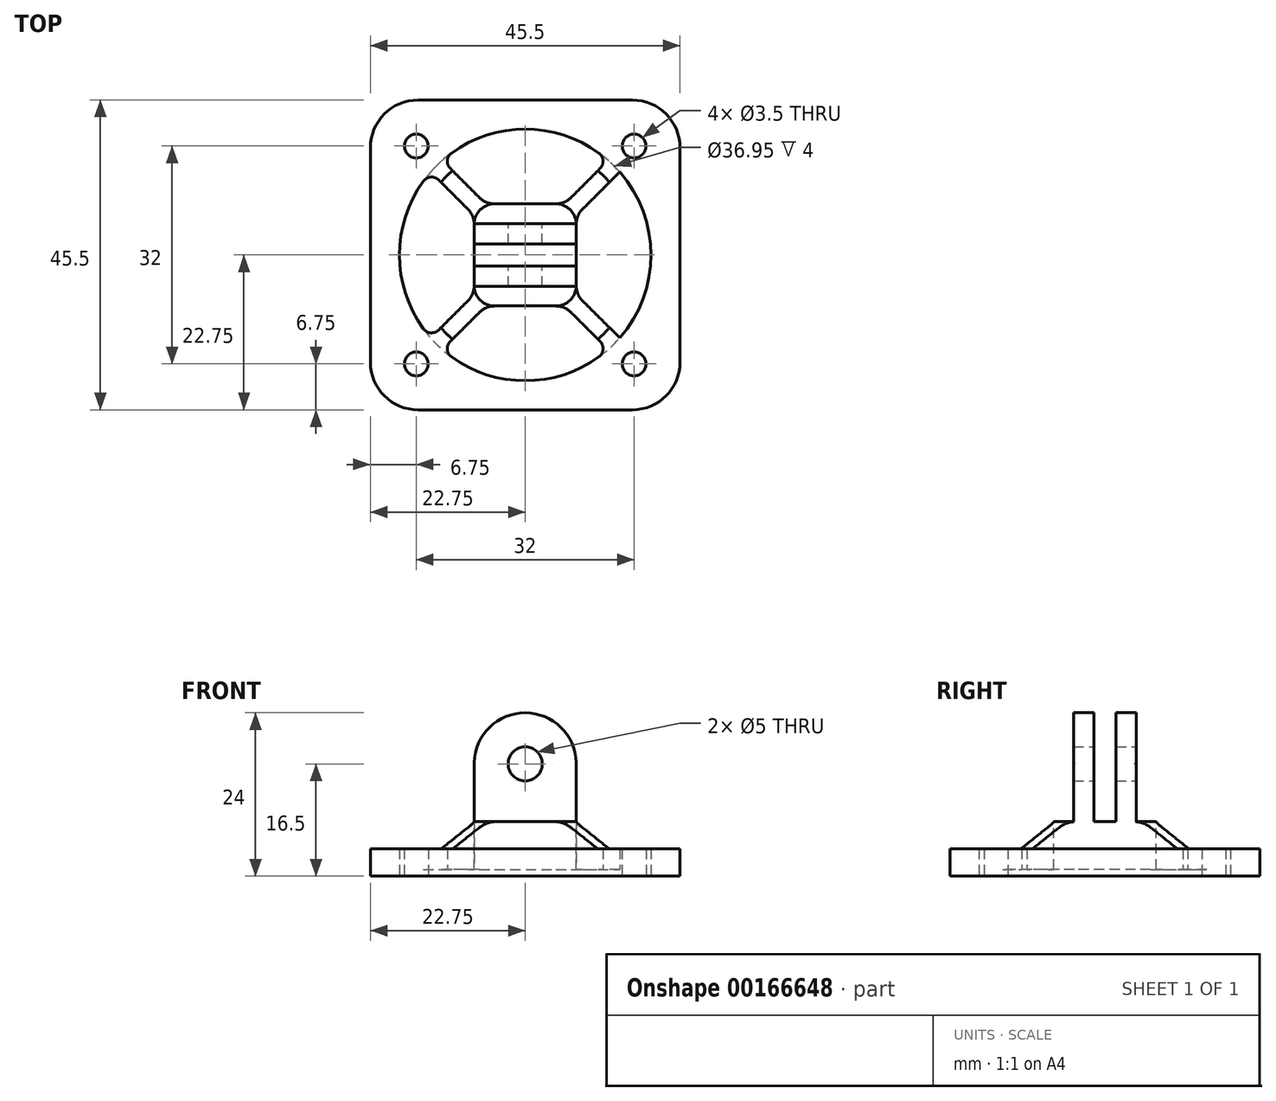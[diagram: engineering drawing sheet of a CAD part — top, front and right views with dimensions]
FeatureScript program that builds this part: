
annotation { "Feature Type Name" : "Feature", "Feature Type Description" : "" }
export const myFeature = defineFeature(function(context is Context, id is Id, definition is map)
    precondition{}
    {
        {
            var Q0;
            Q0=qCreatedBy(makeId("Top.planeOp"),FACE);
            var sketch = newSketch(context, id + "F0", { "sketchPlane" : qUnion([Q0])});
            skLineSegment(sketch, "E0.bottom", {"start": v(16, -16) * mm, "end": v(-16, -16) * mm, "construction": true});
            skLineSegment(sketch, "E0.top", {"start": v(16, 16) * mm, "end": v(-16, 16) * mm, "construction": true});
            skLineSegment(sketch, "E0.left", {"start": v(16, -16) * mm, "end": v(16, 16) * mm, "construction": true});
            skLineSegment(sketch, "E0.right", {"start": v(-16, -16) * mm, "end": v(-16, 16) * mm, "construction": true});
            skPoint(sketch, "E0.middle", {"position": v(0, 0) * mm});
            skLineSegment(sketch, "E1.bottom", {"start": v(22.75, -22.75) * mm, "end": v(-22.75, -22.75) * mm});
            skLineSegment(sketch, "E1.top", {"start": v(22.75, 22.75) * mm, "end": v(-22.75, 22.75) * mm});
            skLineSegment(sketch, "E1.left", {"start": v(22.75, -22.75) * mm, "end": v(22.75, 22.75) * mm});
            skLineSegment(sketch, "E1.right", {"start": v(-22.75, -22.75) * mm, "end": v(-22.75, 22.75) * mm});
            skCircle(sketch, "E2", {"center": v(-16, 16) * mm, "radius": 1.75 * mm, "construction": true});
            skCircle(sketch, "E3", {"center": v(16, 16) * mm, "radius": 1.75 * mm, "construction": true});
            skCircle(sketch, "E4", {"center": v(16, -16) * mm, "radius": 1.75 * mm, "construction": true});
            skCircle(sketch, "E5", {"center": v(-16, -16) * mm, "radius": 1.75 * mm, "construction": true});
            skCircle(sketch, "E6", {"center": v(0, 0) * mm, "radius": 18.48 * mm});
            skCircle(sketch, "E7", {"center": v(0, 0) * mm, "radius": 7.5 * mm});
            skLineSegment(sketch, "E8", {"start": v(0, 0) * mm, "end": v(16, 16) * mm, "construction": true});
            skLineSegment(sketch, "E9", {"start": v(6.08, 4.39) * mm, "end": v(13.89, 12.19) * mm});
            skLineSegment(sketch, "E10.MirrorCS", {"start": v(4.39, 6.08) * mm, "end": v(12.19, 13.89) * mm});
            skLineSegment(sketch, "E11.1.0", {"start": v(6.08, -4.39) * mm, "end": v(13.89, -12.19) * mm});
            skLineSegment(sketch, "E11.1.1", {"start": v(4.39, -6.08) * mm, "end": v(12.19, -13.89) * mm});
            skLineSegment(sketch, "E11.2.0", {"start": v(-4.39, -6.08) * mm, "end": v(-12.19, -13.89) * mm});
            skLineSegment(sketch, "E11.2.1", {"start": v(-6.08, -4.39) * mm, "end": v(-13.89, -12.19) * mm});
            skLineSegment(sketch, "E11.3.0", {"start": v(-6.08, 4.39) * mm, "end": v(-13.89, 12.19) * mm});
            skLineSegment(sketch, "E11.3.1", {"start": v(-4.39, 6.08) * mm, "end": v(-12.19, 13.89) * mm});
            skLineSegment(sketch, "E11.anchor1", {"start": v(0, 0) * mm, "end": v(4.39, 6.08) * mm, "construction": true});
            skLineSegment(sketch, "E11.anchor2", {"start": v(0, 0) * mm, "end": v(-6.08, 4.39) * mm, "construction": true});
            skSolve(sketch);
        }
        {
            var Q0;
            Q0=makeQuery(id+"F0.imprint","IMPRINT",FACE,{"disambiguationData":[TD([[makeQuery(id+"F0.imprint","IMPRINT",EDGE,{"derivedFrom":sQuery(id+"F0.wireOp",EDGE,"E1.bottom")}),-1.0]])]});
            extrude(context, id + "F1", {"entities" : qUnion([Q0]), "depth" : 3 * mm});
        }
        {
            var Q0;
            {var subQ0=sQuery(id+"F0.wireOp",EDGE,"E7");var subQ8=makeQuery(id+"F0.imprint","INTERSECT",VERTEX,{"derivedFrom":[subQ0,sQuery(id+"F0.wireOp",EDGE,"E9")]});Q0=makeQuery(id+"F0.imprint","IMPRINT",FACE,{"disambiguationData":[TD([[makeQuery(id+"F0.imprint","IMPRINT",EDGE,{"disambiguationData":[TD([[subQ8,-1.0]])],"derivedFrom":subQ0}),1.0]])]});}
            var Q1;
            {var subQ0=sQuery(id+"F0.wireOp",EDGE,"E11.3.0");Q1=makeQuery(id+"F0.imprint","IMPRINT",FACE,{"disambiguationData":[TD([[makeQuery(id+"F0.imprint","IMPRINT",EDGE,{"derivedFrom":subQ0}),-1.0]])]});}
            var Q2;
            Q2=makeQuery(id+"F0.imprint","IMPRINT",FACE,{"disambiguationData":[TD([[makeQuery(id+"F0.imprint","IMPRINT",EDGE,{"derivedFrom":sQuery(id+"F0.wireOp",EDGE,"E1.bottom")}),-1.0]])]});
            var Q3;
            {var subQ0=sQuery(id+"F0.wireOp",EDGE,"E9");Q3=makeQuery(id+"F0.imprint","IMPRINT",FACE,{"disambiguationData":[TD([[makeQuery(id+"F0.imprint","IMPRINT",EDGE,{"derivedFrom":subQ0}),1.0]])]});}
            var Q4;
            {var subQ0=sQuery(id+"F0.wireOp",EDGE,"E11.1.0");Q4=makeQuery(id+"F0.imprint","IMPRINT",FACE,{"disambiguationData":[TD([[makeQuery(id+"F0.imprint","IMPRINT",EDGE,{"derivedFrom":subQ0}),-1.0]])]});}
            var Q5;
            {var subQ0=sQuery(id+"F0.wireOp",EDGE,"E11.2.0");Q5=makeQuery(id+"F0.imprint","IMPRINT",FACE,{"disambiguationData":[TD([[makeQuery(id+"F0.imprint","IMPRINT",EDGE,{"derivedFrom":subQ0}),-1.0]])]});}
            extrude(context, id + "F2", {"entities" : qUnion([Q0, Q1, Q2, Q3, Q4, Q5]), "operationType" : NewBodyOperationType.ADD, "depth" : 3 * mm});
        }
        {
            var Q0;
            Q0=makeQuery(id+"F0.imprint","IMPRINT",FACE,{"disambiguationData":[TD([[makeQuery(id+"F0.imprint","IMPRINT",EDGE,{"derivedFrom":sQuery(id+"F0.wireOp",EDGE,"E1.bottom")}),-1.0]])]});
            extrude(context, id + "F3", {"entities" : qUnion([Q0]), "operationType" : NewBodyOperationType.ADD, "oppositeDirection" : true, "depth" : 1 * mm});
        }
        {
            var Q0;
            Q0=makeQuery(id+"F3.opExtrude","CAP_FACE",FACE,{"disambiguationData":[OSD([sQuery(id+"F0.wireOp",EDGE,"E1.bottom"),sQuery(id+"F0.wireOp",EDGE,"E1.top"),sQuery(id+"F0.wireOp",EDGE,"E1.left"),sQuery(id+"F0.wireOp",EDGE,"E1.right"),sQuery(id+"F0.wireOp",EDGE,"E6")])],"isStart":false});
            var sketch = newSketch(context, id + "F4", { "sketchPlane" : qUnion([Q0])});
            skPoint(sketch, "E12.0", {"position": v(-16, 16) * mm});
            skPoint(sketch, "E12.1", {"position": v(16, 16) * mm});
            skPoint(sketch, "E12.2", {"position": v(16, -16) * mm});
            skPoint(sketch, "E12.3", {"position": v(-16, -16) * mm});
            skSolve(sketch);
        }
        {
            var Q0;
            Q0=sQuery(id+"F4.wireOp",VERTEX,"E12.0");
            var Q1;
            Q1=sQuery(id+"F4.wireOp",VERTEX,"E12.3");
            var Q2;
            Q2=sQuery(id+"F4.wireOp",VERTEX,"E12.2");
            var Q3;
            Q3=sQuery(id+"F4.wireOp",VERTEX,"E12.1");
            var Q4;
            Q4=makeQuery(id+"F1.opExtrude","SWEPT_BODY",BODY,{"disambiguationData":[OSD([sQuery(id+"F0.wireOp",EDGE,"E1.bottom"),sQuery(id+"F0.wireOp",EDGE,"E1.top"),sQuery(id+"F0.wireOp",EDGE,"E1.left"),sQuery(id+"F0.wireOp",EDGE,"E1.right"),sQuery(id+"F0.wireOp",EDGE,"E6")])]});
            hole(context, id + "F5", {"style" : HoleStyle.SIMPLE, "endStyle" : HoleEndStyle.THROUGH, "holeDiameter" : 3.5 * mm, "locations" : qUnion([Q0, Q1, Q2, Q3]), "scope" : qUnion([Q4]), "isTappedThrough" : true});
        }
        {
            var Q0;
            Q0=makeQuery(id+"F2.opExtrude","SWEPT_EDGE",EDGE,{"disambiguationData":[OSD([sQuery(id+"F0.wireOp",EDGE,"E7"),sQuery(id+"F0.wireOp",EDGE,"E11.1.1")])]});
            var Q1;
            Q1=makeQuery(id+"F2.opExtrude","SWEPT_EDGE",EDGE,{"disambiguationData":[OSD([sQuery(id+"F0.wireOp",EDGE,"E7"),sQuery(id+"F0.wireOp",EDGE,"E11.2.0")])]});
            var Q2;
            Q2=makeQuery(id+"F2.opExtrude","SWEPT_EDGE",EDGE,{"disambiguationData":[OSD([sQuery(id+"F0.wireOp",EDGE,"E7"),sQuery(id+"F0.wireOp",EDGE,"E11.2.1")])]});
            var Q3;
            Q3=makeQuery(id+"F2.opExtrude","SWEPT_EDGE",EDGE,{"disambiguationData":[OSD([sQuery(id+"F0.wireOp",EDGE,"E7"),sQuery(id+"F0.wireOp",EDGE,"E11.3.0")])]});
            var Q4;
            Q4=makeQuery(id+"F2.opExtrude","SWEPT_EDGE",EDGE,{"disambiguationData":[OSD([sQuery(id+"F0.wireOp",EDGE,"E7"),sQuery(id+"F0.wireOp",EDGE,"E11.3.1")])]});
            var Q5;
            Q5=makeQuery(id+"F2.opExtrude","SWEPT_EDGE",EDGE,{"disambiguationData":[OSD([sQuery(id+"F0.wireOp",EDGE,"E7"),sQuery(id+"F0.wireOp",EDGE,"E10.MirrorCS")])]});
            var Q6;
            Q6=makeQuery(id+"F2.opExtrude","SWEPT_EDGE",EDGE,{"disambiguationData":[OSD([sQuery(id+"F0.wireOp",EDGE,"E7"),sQuery(id+"F0.wireOp",EDGE,"E9")])]});
            var Q7;
            Q7=makeQuery(id+"F2.opExtrude","SWEPT_EDGE",EDGE,{"disambiguationData":[OSD([sQuery(id+"F0.wireOp",EDGE,"E7"),sQuery(id+"F0.wireOp",EDGE,"E11.1.0")])]});
            var Q8;
            Q8=makeQuery(id+"F2.opExtrude","SWEPT_EDGE",EDGE,{"disambiguationData":[OSD([sQuery(id+"F0.wireOp",EDGE,"E6"),sQuery(id+"F0.wireOp",EDGE,"E11.3.1")])]});
            var Q9;
            Q9=makeQuery(id+"F2.opExtrude","SWEPT_EDGE",EDGE,{"disambiguationData":[OSD([sQuery(id+"F0.wireOp",EDGE,"E6"),sQuery(id+"F0.wireOp",EDGE,"E11.3.0")])]});
            var Q10;
            Q10=makeQuery(id+"F2.opExtrude","SWEPT_EDGE",EDGE,{"disambiguationData":[OSD([sQuery(id+"F0.wireOp",EDGE,"E6"),sQuery(id+"F0.wireOp",EDGE,"E11.2.1")])]});
            var Q11;
            Q11=makeQuery(id+"F2.opExtrude","SWEPT_EDGE",EDGE,{"disambiguationData":[OSD([sQuery(id+"F0.wireOp",EDGE,"E6"),sQuery(id+"F0.wireOp",EDGE,"E11.2.0")])]});
            var Q12;
            Q12=makeQuery(id+"F2.opExtrude","SWEPT_EDGE",EDGE,{"disambiguationData":[OSD([sQuery(id+"F0.wireOp",EDGE,"E6"),sQuery(id+"F0.wireOp",EDGE,"E11.1.0")])]});
            var Q13;
            Q13=makeQuery(id+"F2.opExtrude","SWEPT_EDGE",EDGE,{"disambiguationData":[OSD([sQuery(id+"F0.wireOp",EDGE,"E6"),sQuery(id+"F0.wireOp",EDGE,"E11.1.1")])]});
            var Q14;
            Q14=makeQuery(id+"F2.opExtrude","SWEPT_EDGE",EDGE,{"disambiguationData":[OSD([sQuery(id+"F0.wireOp",EDGE,"E6"),sQuery(id+"F0.wireOp",EDGE,"E9")])]});
            var Q15;
            Q15=makeQuery(id+"F2.opExtrude","SWEPT_EDGE",EDGE,{"disambiguationData":[OSD([sQuery(id+"F0.wireOp",EDGE,"E6"),sQuery(id+"F0.wireOp",EDGE,"E10.MirrorCS")])]});
            fillet(context, id + "F6", {"entities" : qUnion([Q0, Q1, Q2, Q3, Q4, Q5, Q6, Q7, Q8, Q9, Q10, Q11, Q12, Q13, Q14, Q15]), "radius" : 1.5 * mm, "tangentPropagation" : true, "allowEdgeOverflow" : false});
        }
        {
            var Q0;
            {var subQ0=sQuery(id+"F0.wireOp",EDGE,"E1.right");var subQ1=sQuery(id+"F0.wireOp",EDGE,"E1.top");Q0=makeQuery(id+"F3.boolean.opBoolean","MERGE",EDGE,{"derivedFrom":[makeQuery(id+"F1.opExtrude","SWEPT_EDGE",EDGE,{"disambiguationData":[OSD([subQ1,subQ0])]}),makeQuery(id+"F3.opExtrude","SWEPT_EDGE",EDGE,{"disambiguationData":[OSD([subQ1,subQ0])]})]});}
            var Q1;
            {var subQ0=sQuery(id+"F0.wireOp",EDGE,"E1.left");var subQ1=sQuery(id+"F0.wireOp",EDGE,"E1.top");Q1=makeQuery(id+"F3.boolean.opBoolean","MERGE",EDGE,{"derivedFrom":[makeQuery(id+"F1.opExtrude","SWEPT_EDGE",EDGE,{"disambiguationData":[OSD([subQ1,subQ0])]}),makeQuery(id+"F3.opExtrude","SWEPT_EDGE",EDGE,{"disambiguationData":[OSD([subQ1,subQ0])]})]});}
            var Q2;
            {var subQ0=sQuery(id+"F0.wireOp",EDGE,"E1.left");var subQ1=sQuery(id+"F0.wireOp",EDGE,"E1.bottom");Q2=makeQuery(id+"F3.boolean.opBoolean","MERGE",EDGE,{"derivedFrom":[makeQuery(id+"F1.opExtrude","SWEPT_EDGE",EDGE,{"disambiguationData":[OSD([subQ1,subQ0])]}),makeQuery(id+"F3.opExtrude","SWEPT_EDGE",EDGE,{"disambiguationData":[OSD([subQ1,subQ0])]})]});}
            var Q3;
            {var subQ0=sQuery(id+"F0.wireOp",EDGE,"E1.right");var subQ1=sQuery(id+"F0.wireOp",EDGE,"E1.bottom");Q3=makeQuery(id+"F3.boolean.opBoolean","MERGE",EDGE,{"derivedFrom":[makeQuery(id+"F1.opExtrude","SWEPT_EDGE",EDGE,{"disambiguationData":[OSD([subQ1,subQ0])]}),makeQuery(id+"F3.opExtrude","SWEPT_EDGE",EDGE,{"disambiguationData":[OSD([subQ1,subQ0])]})]});}
            fillet(context, id + "F7", {"entities" : qUnion([Q0, Q1, Q2, Q3]), "radius" : 7 * mm, "tangentPropagation" : true, "allowEdgeOverflow" : false});
        }
        {
            var Q0;
            Q0=qCreatedBy(makeId("Front.planeOp"),FACE);
            var sketch = newSketch(context, id + "F8", { "sketchPlane" : qUnion([Q0])});
            skLineSegment(sketch, "E13.0", {"start": v(15.75, 3) * mm, "end": v(-15.75, 3) * mm});
            skLineSegment(sketch, "E14", {"start": v(-7.5, 3) * mm, "end": v(-7.5, 15.5) * mm});
            skLineSegment(sketch, "E15", {"start": v(7.5, 3) * mm, "end": v(7.5, 15.5) * mm});
            skArc(sketch, "E16", {"start": v(7.5, 15.5) * mm, "mid": v(0, 23) * mm, "end": v(-7.5, 15.5) * mm});
            skCircle(sketch, "E17", {"center": v(0, 15.5) * mm, "radius": 2.5 * mm});
            skSolve(sketch);
        }
        {
            var Q0;
            {var subQ0=sQuery(id+"F8.wireOp",EDGE,"E14");Q0=makeQuery(id+"F8.imprint","IMPRINT",FACE,{"disambiguationData":[TD([[makeQuery(id+"F8.imprint","IMPRINT",EDGE,{"derivedFrom":subQ0}),-1.0]])]});}
            extrude(context, id + "F9", {"entities" : qUnion([Q0]), "operationType" : NewBodyOperationType.ADD, "endBound" : BoundingType.SYMMETRIC, "depth" : 15 * mm});
        }
        {
            var Q0;
            Q0=makeQuery(id+"F9.opExtrude","CAP_EDGE",EDGE,{"disambiguationData":[OSD([sQuery(id+"F8.wireOp",EDGE,"E16")])],"isStart":false});
            cPoint(context, id + "F10", {"entities" : qUnion([Q0]), "parameter" : 0.5});
        }
        {
            var Q0;
            Q0=qCreatedBy(makeId("Top.planeOp"),FACE);
            var Q1;
            Q1 = qCreatedBy(id + "F10" ,VERTEX);
            cPlane(context, id + "F11", {"entities" : qUnion([Q0, Q1]), "cplaneType" : CPlaneType.PLANE_POINT, "offset" : 25 * mm, "width" : 150 * mm, "height" : 150 * mm});
        }
        {
            var Q0;
            Q0=qCreatedBy(id+"F11.planeOp",FACE);
            var sketch = newSketch(context, id + "F12", { "sketchPlane" : qUnion([Q0])});
            skLineSegment(sketch, "E18.0.0", {"start": v(7.5, 7.5) * mm, "end": v(-7.5, 7.5) * mm});
            skLineSegment(sketch, "E18.0.1", {"start": v(-7.5, 7.5) * mm, "end": v(-7.5, -7.5) * mm});
            skLineSegment(sketch, "E18.0.2", {"start": v(-7.5, -7.5) * mm, "end": v(7.5, -7.5) * mm});
            skLineSegment(sketch, "E18.0.3", {"start": v(7.5, -7.5) * mm, "end": v(7.5, 7.5) * mm});
            skLineSegment(sketch, "E19", {"start": v(7.5, 1.63) * mm, "end": v(-7.5, 1.62) * mm});
            skLineSegment(sketch, "E20", {"start": v(7.5, -1.63) * mm, "end": v(-7.5, -1.62) * mm});
            skLineSegment(sketch, "E21", {"start": v(7.5, -4.63) * mm, "end": v(-7.5, -4.62) * mm});
            skLineSegment(sketch, "E22", {"start": v(7.5, 4.63) * mm, "end": v(-7.5, 4.62) * mm});
            skSolve(sketch);
        }
        {
            var Q0;
            {var subQ0=sQuery(id+"F12.wireOp",EDGE,"E19");Q0=makeQuery(id+"F12.imprint","IMPRINT",FACE,{"disambiguationData":[TD([[makeQuery(id+"F12.imprint","IMPRINT",EDGE,{"derivedFrom":subQ0}),1.0]])]});}
            var Q1;
            {var subQ0=sQuery(id+"F12.wireOp",EDGE,"E18.0.2");Q1=makeQuery(id+"F12.imprint","IMPRINT",FACE,{"disambiguationData":[TD([[makeQuery(id+"F12.imprint","IMPRINT",EDGE,{"derivedFrom":subQ0}),1.0]])]});}
            var Q2;
            {var subQ0=sQuery(id+"F12.wireOp",EDGE,"E18.0.0");Q2=makeQuery(id+"F12.imprint","IMPRINT",FACE,{"disambiguationData":[TD([[makeQuery(id+"F12.imprint","IMPRINT",EDGE,{"derivedFrom":subQ0}),1.0]])]});}
            extrude(context, id + "F13", {"entities" : qUnion([Q0, Q1, Q2]), "operationType" : NewBodyOperationType.REMOVE, "oppositeDirection" : true, "depth" : 16 * mm});
        }
        {
            var Q0;
            Q0=makeQuery(id+"F9.opExtrude","CAP_EDGE",EDGE,{"disambiguationData":[OSD([sQuery(id+"F8.wireOp",EDGE,"E14")])],"isStart":false});
            var Q1;
            Q1=makeQuery(id+"F9.opExtrude","CAP_EDGE",EDGE,{"disambiguationData":[OSD([sQuery(id+"F8.wireOp",EDGE,"E15")])],"isStart":false});
            var Q2;
            Q2=makeQuery(id+"F9.opExtrude","CAP_EDGE",EDGE,{"disambiguationData":[OSD([sQuery(id+"F8.wireOp",EDGE,"E15")])],"isStart":true});
            var Q3;
            Q3=makeQuery(id+"F9.opExtrude","CAP_EDGE",EDGE,{"disambiguationData":[OSD([sQuery(id+"F8.wireOp",EDGE,"E14")])],"isStart":true});
            fillet(context, id + "F14", {"entities" : qUnion([Q0, Q1, Q2, Q3]), "radius" : 3 * mm, "tangentPropagation" : true, "allowEdgeOverflow" : false});
        }
        {
            var Q0;
            {var subQ0=sQuery(id+"F0.wireOp",EDGE,"E6");var subQ1=sQuery(id+"F0.wireOp",EDGE,"E1.right");var subQ2=sQuery(id+"F0.wireOp",EDGE,"E1.left");var subQ3=sQuery(id+"F0.wireOp",EDGE,"E1.top");var subQ4=sQuery(id+"F0.wireOp",EDGE,"E1.bottom");Q0=makeQuery(id+"F14.opFillet","BLEND_EDGE",EDGE,{"blendedFrom":[makeQuery(id+"F9.opExtrude","CAP_EDGE",EDGE,{"disambiguationData":[OSD([sQuery(id+"F8.wireOp",EDGE,"E15")])],"isStart":false}),makeQuery(id+"F2.boolean.opBoolean","MERGE",FACE,{"derivedFrom":[makeQuery(id+"F1.opExtrude","CAP_FACE",FACE,{"disambiguationData":[OSD([subQ4,subQ3,subQ2,subQ1,subQ0])],"isStart":false}),makeQuery(id+"F2.opExtrude","CAP_FACE",FACE,{"disambiguationData":[OSD([subQ4,subQ3,subQ2,subQ1,subQ0,sQuery(id+"F0.wireOp",EDGE,"E7"),sQuery(id+"F0.wireOp",EDGE,"E9"),sQuery(id+"F0.wireOp",EDGE,"E10.MirrorCS"),sQuery(id+"F0.wireOp",EDGE,"E11.1.0"),sQuery(id+"F0.wireOp",EDGE,"E11.1.1"),sQuery(id+"F0.wireOp",EDGE,"E11.2.0"),sQuery(id+"F0.wireOp",EDGE,"E11.2.1"),sQuery(id+"F0.wireOp",EDGE,"E11.3.0"),sQuery(id+"F0.wireOp",EDGE,"E11.3.1")])],"isStart":false})]})],"blendedInto":[makeQuery(id+"F2.boolean.opBoolean","MERGE",FACE,{"derivedFrom":[makeQuery(id+"F1.opExtrude","CAP_FACE",FACE,{"disambiguationData":[OSD([subQ4,subQ3,subQ2,subQ1,subQ0])],"isStart":false}),makeQuery(id+"F2.opExtrude","CAP_FACE",FACE,{"disambiguationData":[OSD([subQ4,subQ3,subQ2,subQ1,subQ0,sQuery(id+"F0.wireOp",EDGE,"E7"),sQuery(id+"F0.wireOp",EDGE,"E9"),sQuery(id+"F0.wireOp",EDGE,"E10.MirrorCS"),sQuery(id+"F0.wireOp",EDGE,"E11.1.0"),sQuery(id+"F0.wireOp",EDGE,"E11.1.1"),sQuery(id+"F0.wireOp",EDGE,"E11.2.0"),sQuery(id+"F0.wireOp",EDGE,"E11.2.1"),sQuery(id+"F0.wireOp",EDGE,"E11.3.0"),sQuery(id+"F0.wireOp",EDGE,"E11.3.1")])],"isStart":false})]})]});}
            var Q1;
            {var subQ0=sQuery(id+"F0.wireOp",EDGE,"E6");var subQ1=sQuery(id+"F0.wireOp",EDGE,"E1.right");var subQ2=sQuery(id+"F0.wireOp",EDGE,"E1.left");var subQ3=sQuery(id+"F0.wireOp",EDGE,"E1.top");var subQ4=sQuery(id+"F0.wireOp",EDGE,"E1.bottom");Q1=makeQuery(id+"F14.opFillet","BLEND_EDGE",EDGE,{"blendedFrom":[makeQuery(id+"F9.opExtrude","CAP_EDGE",EDGE,{"disambiguationData":[OSD([sQuery(id+"F8.wireOp",EDGE,"E15")])],"isStart":true}),makeQuery(id+"F2.boolean.opBoolean","MERGE",FACE,{"derivedFrom":[makeQuery(id+"F1.opExtrude","CAP_FACE",FACE,{"disambiguationData":[OSD([subQ4,subQ3,subQ2,subQ1,subQ0])],"isStart":false}),makeQuery(id+"F2.opExtrude","CAP_FACE",FACE,{"disambiguationData":[OSD([subQ4,subQ3,subQ2,subQ1,subQ0,sQuery(id+"F0.wireOp",EDGE,"E7"),sQuery(id+"F0.wireOp",EDGE,"E9"),sQuery(id+"F0.wireOp",EDGE,"E10.MirrorCS"),sQuery(id+"F0.wireOp",EDGE,"E11.1.0"),sQuery(id+"F0.wireOp",EDGE,"E11.1.1"),sQuery(id+"F0.wireOp",EDGE,"E11.2.0"),sQuery(id+"F0.wireOp",EDGE,"E11.2.1"),sQuery(id+"F0.wireOp",EDGE,"E11.3.0"),sQuery(id+"F0.wireOp",EDGE,"E11.3.1")])],"isStart":false})]})],"blendedInto":[makeQuery(id+"F2.boolean.opBoolean","MERGE",FACE,{"derivedFrom":[makeQuery(id+"F1.opExtrude","CAP_FACE",FACE,{"disambiguationData":[OSD([subQ4,subQ3,subQ2,subQ1,subQ0])],"isStart":false}),makeQuery(id+"F2.opExtrude","CAP_FACE",FACE,{"disambiguationData":[OSD([subQ4,subQ3,subQ2,subQ1,subQ0,sQuery(id+"F0.wireOp",EDGE,"E7"),sQuery(id+"F0.wireOp",EDGE,"E9"),sQuery(id+"F0.wireOp",EDGE,"E10.MirrorCS"),sQuery(id+"F0.wireOp",EDGE,"E11.1.0"),sQuery(id+"F0.wireOp",EDGE,"E11.1.1"),sQuery(id+"F0.wireOp",EDGE,"E11.2.0"),sQuery(id+"F0.wireOp",EDGE,"E11.2.1"),sQuery(id+"F0.wireOp",EDGE,"E11.3.0"),sQuery(id+"F0.wireOp",EDGE,"E11.3.1")])],"isStart":false})]})]});}
            var Q2;
            {var subQ0=sQuery(id+"F0.wireOp",EDGE,"E6");var subQ1=sQuery(id+"F0.wireOp",EDGE,"E1.right");var subQ2=sQuery(id+"F0.wireOp",EDGE,"E1.left");var subQ3=sQuery(id+"F0.wireOp",EDGE,"E1.top");var subQ4=sQuery(id+"F0.wireOp",EDGE,"E1.bottom");Q2=makeQuery(id+"F14.opFillet","BLEND_EDGE",EDGE,{"blendedFrom":[makeQuery(id+"F9.opExtrude","CAP_EDGE",EDGE,{"disambiguationData":[OSD([sQuery(id+"F8.wireOp",EDGE,"E14")])],"isStart":true}),makeQuery(id+"F2.boolean.opBoolean","MERGE",FACE,{"derivedFrom":[makeQuery(id+"F1.opExtrude","CAP_FACE",FACE,{"disambiguationData":[OSD([subQ4,subQ3,subQ2,subQ1,subQ0])],"isStart":false}),makeQuery(id+"F2.opExtrude","CAP_FACE",FACE,{"disambiguationData":[OSD([subQ4,subQ3,subQ2,subQ1,subQ0,sQuery(id+"F0.wireOp",EDGE,"E7"),sQuery(id+"F0.wireOp",EDGE,"E9"),sQuery(id+"F0.wireOp",EDGE,"E10.MirrorCS"),sQuery(id+"F0.wireOp",EDGE,"E11.1.0"),sQuery(id+"F0.wireOp",EDGE,"E11.1.1"),sQuery(id+"F0.wireOp",EDGE,"E11.2.0"),sQuery(id+"F0.wireOp",EDGE,"E11.2.1"),sQuery(id+"F0.wireOp",EDGE,"E11.3.0"),sQuery(id+"F0.wireOp",EDGE,"E11.3.1")])],"isStart":false})]})],"blendedInto":[makeQuery(id+"F2.boolean.opBoolean","MERGE",FACE,{"derivedFrom":[makeQuery(id+"F1.opExtrude","CAP_FACE",FACE,{"disambiguationData":[OSD([subQ4,subQ3,subQ2,subQ1,subQ0])],"isStart":false}),makeQuery(id+"F2.opExtrude","CAP_FACE",FACE,{"disambiguationData":[OSD([subQ4,subQ3,subQ2,subQ1,subQ0,sQuery(id+"F0.wireOp",EDGE,"E7"),sQuery(id+"F0.wireOp",EDGE,"E9"),sQuery(id+"F0.wireOp",EDGE,"E10.MirrorCS"),sQuery(id+"F0.wireOp",EDGE,"E11.1.0"),sQuery(id+"F0.wireOp",EDGE,"E11.1.1"),sQuery(id+"F0.wireOp",EDGE,"E11.2.0"),sQuery(id+"F0.wireOp",EDGE,"E11.2.1"),sQuery(id+"F0.wireOp",EDGE,"E11.3.0"),sQuery(id+"F0.wireOp",EDGE,"E11.3.1")])],"isStart":false})]})]});}
            var Q3;
            {var subQ0=sQuery(id+"F0.wireOp",EDGE,"E6");var subQ1=sQuery(id+"F0.wireOp",EDGE,"E1.right");var subQ2=sQuery(id+"F0.wireOp",EDGE,"E1.left");var subQ3=sQuery(id+"F0.wireOp",EDGE,"E1.top");var subQ4=sQuery(id+"F0.wireOp",EDGE,"E1.bottom");Q3=makeQuery(id+"F14.opFillet","BLEND_EDGE",EDGE,{"blendedFrom":[makeQuery(id+"F9.opExtrude","CAP_EDGE",EDGE,{"disambiguationData":[OSD([sQuery(id+"F8.wireOp",EDGE,"E14")])],"isStart":false}),makeQuery(id+"F2.boolean.opBoolean","MERGE",FACE,{"derivedFrom":[makeQuery(id+"F1.opExtrude","CAP_FACE",FACE,{"disambiguationData":[OSD([subQ4,subQ3,subQ2,subQ1,subQ0])],"isStart":false}),makeQuery(id+"F2.opExtrude","CAP_FACE",FACE,{"disambiguationData":[OSD([subQ4,subQ3,subQ2,subQ1,subQ0,sQuery(id+"F0.wireOp",EDGE,"E7"),sQuery(id+"F0.wireOp",EDGE,"E9"),sQuery(id+"F0.wireOp",EDGE,"E10.MirrorCS"),sQuery(id+"F0.wireOp",EDGE,"E11.1.0"),sQuery(id+"F0.wireOp",EDGE,"E11.1.1"),sQuery(id+"F0.wireOp",EDGE,"E11.2.0"),sQuery(id+"F0.wireOp",EDGE,"E11.2.1"),sQuery(id+"F0.wireOp",EDGE,"E11.3.0"),sQuery(id+"F0.wireOp",EDGE,"E11.3.1")])],"isStart":false})]})],"blendedInto":[makeQuery(id+"F2.boolean.opBoolean","MERGE",FACE,{"derivedFrom":[makeQuery(id+"F1.opExtrude","CAP_FACE",FACE,{"disambiguationData":[OSD([subQ4,subQ3,subQ2,subQ1,subQ0])],"isStart":false}),makeQuery(id+"F2.opExtrude","CAP_FACE",FACE,{"disambiguationData":[OSD([subQ4,subQ3,subQ2,subQ1,subQ0,sQuery(id+"F0.wireOp",EDGE,"E7"),sQuery(id+"F0.wireOp",EDGE,"E9"),sQuery(id+"F0.wireOp",EDGE,"E10.MirrorCS"),sQuery(id+"F0.wireOp",EDGE,"E11.1.0"),sQuery(id+"F0.wireOp",EDGE,"E11.1.1"),sQuery(id+"F0.wireOp",EDGE,"E11.2.0"),sQuery(id+"F0.wireOp",EDGE,"E11.2.1"),sQuery(id+"F0.wireOp",EDGE,"E11.3.0"),sQuery(id+"F0.wireOp",EDGE,"E11.3.1")])],"isStart":false})]})]});}
            chamfer(context, id + "F15", {"entities" : qUnion([Q0, Q1, Q2, Q3]), "chamferType" : ChamferType.TWO_OFFSETS, "width1" : 7 * mm, "oppositeDirection" : false, "width2" : 4 * mm, "tangentPropagation" : true});
        }
        {
            var Q0;
            {var subQ0=sQuery(id+"F0.wireOp",EDGE,"E11.2.0");var subQ1=makeQuery(id+"F2.opExtrude","SWEPT_FACE",FACE,{"disambiguationData":[OSD([subQ0])]});var subQ2=sQuery(id+"F8.wireOp",EDGE,"E13.0");var subQ3=makeQuery(id+"F9.opExtrude","SWEPT_FACE",FACE,{"disambiguationData":[OSD([subQ2])]});var subQ4=sQuery(id+"F0.wireOp",EDGE,"E11.1.1");var subQ5=sQuery(id+"F0.wireOp",EDGE,"E7");var subQ6=sQuery(id+"F0.wireOp",EDGE,"E6");var subQ7=sQuery(id+"F0.wireOp",EDGE,"E1.right");var subQ8=sQuery(id+"F0.wireOp",EDGE,"E1.left");var subQ9=sQuery(id+"F0.wireOp",EDGE,"E1.top");var subQ10=sQuery(id+"F0.wireOp",EDGE,"E1.bottom");var subQ11=makeQuery(id+"F2.opExtrude","CAP_FACE",FACE,{"disambiguationData":[OSD([subQ10,subQ9,subQ8,subQ7,subQ6,subQ5,sQuery(id+"F0.wireOp",EDGE,"E9"),sQuery(id+"F0.wireOp",EDGE,"E10.MirrorCS"),sQuery(id+"F0.wireOp",EDGE,"E11.1.0"),subQ4,subQ0,sQuery(id+"F0.wireOp",EDGE,"E11.2.1"),sQuery(id+"F0.wireOp",EDGE,"E11.3.0"),sQuery(id+"F0.wireOp",EDGE,"E11.3.1")])],"isStart":false});var subQ12=makeQuery(id+"F1.opExtrude","CAP_FACE",FACE,{"disambiguationData":[OSD([subQ10,subQ9,subQ8,subQ7,subQ6])],"isStart":false});var subQ13=sQuery(id+"F8.wireOp",EDGE,"E14");Q0=makeQuery(id+"F15.opChamfer","TWEAK_EDGE",EDGE,{"derivedFrom":[makeQuery(id+"F14.opFillet","BLEND_VERTEX",VERTEX,{"blendedFrom":[makeQuery(id+"F9.opExtrude","CAP_EDGE",EDGE,{"disambiguationData":[OSD([subQ13])],"isStart":false}),subQ1,makeQuery(id+"F2.boolean.opBoolean","MERGE",FACE,{"derivedFrom":[subQ12,subQ11]}),makeQuery(id+"F9.boolean.opBoolean","SPLIT",FACE,{"disambiguationData":[TD([subQ1])],"derivedFrom":subQ3})],"blendedInto":[subQ1,makeQuery(id+"F2.boolean.opBoolean","MERGE",FACE,{"derivedFrom":[subQ12,subQ11]}),makeQuery(id+"F9.boolean.opBoolean","SPLIT",FACE,{"disambiguationData":[TD([subQ1])],"derivedFrom":subQ3})]})]});}
            var Q1;
            {var subQ0=sQuery(id+"F0.wireOp",EDGE,"E11.1.1");var subQ1=makeQuery(id+"F2.opExtrude","SWEPT_FACE",FACE,{"disambiguationData":[OSD([subQ0])]});var subQ2=sQuery(id+"F0.wireOp",EDGE,"E7");var subQ3=sQuery(id+"F0.wireOp",EDGE,"E11.2.0");var subQ4=sQuery(id+"F0.wireOp",EDGE,"E6");var subQ5=sQuery(id+"F0.wireOp",EDGE,"E1.right");var subQ6=sQuery(id+"F0.wireOp",EDGE,"E1.left");var subQ7=sQuery(id+"F0.wireOp",EDGE,"E1.top");var subQ8=sQuery(id+"F0.wireOp",EDGE,"E1.bottom");var subQ9=makeQuery(id+"F2.opExtrude","CAP_FACE",FACE,{"disambiguationData":[OSD([subQ8,subQ7,subQ6,subQ5,subQ4,subQ2,sQuery(id+"F0.wireOp",EDGE,"E9"),sQuery(id+"F0.wireOp",EDGE,"E10.MirrorCS"),sQuery(id+"F0.wireOp",EDGE,"E11.1.0"),subQ0,subQ3,sQuery(id+"F0.wireOp",EDGE,"E11.2.1"),sQuery(id+"F0.wireOp",EDGE,"E11.3.0"),sQuery(id+"F0.wireOp",EDGE,"E11.3.1")])],"isStart":false});var subQ10=makeQuery(id+"F1.opExtrude","CAP_FACE",FACE,{"disambiguationData":[OSD([subQ8,subQ7,subQ6,subQ5,subQ4])],"isStart":false});var subQ11=sQuery(id+"F8.wireOp",EDGE,"E13.0");var subQ12=makeQuery(id+"F9.opExtrude","SWEPT_FACE",FACE,{"disambiguationData":[OSD([subQ11])]});var subQ13=sQuery(id+"F8.wireOp",EDGE,"E15");Q1=makeQuery(id+"F15.opChamfer","TWEAK_EDGE",EDGE,{"derivedFrom":[makeQuery(id+"F14.opFillet","BLEND_VERTEX",VERTEX,{"blendedFrom":[makeQuery(id+"F9.opExtrude","CAP_EDGE",EDGE,{"disambiguationData":[OSD([subQ13])],"isStart":false}),subQ1,makeQuery(id+"F2.boolean.opBoolean","MERGE",FACE,{"derivedFrom":[subQ10,subQ9]}),makeQuery(id+"F9.boolean.opBoolean","SPLIT",FACE,{"disambiguationData":[TD([subQ1])],"derivedFrom":subQ12})],"blendedInto":[subQ1,makeQuery(id+"F2.boolean.opBoolean","MERGE",FACE,{"derivedFrom":[subQ10,subQ9]}),makeQuery(id+"F9.boolean.opBoolean","SPLIT",FACE,{"disambiguationData":[TD([subQ1])],"derivedFrom":subQ12})]})]});}
            var Q2;
            {var subQ0=sQuery(id+"F0.wireOp",EDGE,"E11.2.1");var subQ1=sQuery(id+"F0.wireOp",EDGE,"E7");var subQ2=sQuery(id+"F0.wireOp",EDGE,"E11.3.0");var subQ3=makeQuery(id+"F2.opExtrude","SWEPT_FACE",FACE,{"disambiguationData":[OSD([subQ0])]});var subQ4=sQuery(id+"F0.wireOp",EDGE,"E6");var subQ5=sQuery(id+"F0.wireOp",EDGE,"E1.right");var subQ6=sQuery(id+"F0.wireOp",EDGE,"E1.left");var subQ7=sQuery(id+"F0.wireOp",EDGE,"E1.top");var subQ8=sQuery(id+"F0.wireOp",EDGE,"E1.bottom");var subQ9=makeQuery(id+"F2.opExtrude","CAP_FACE",FACE,{"disambiguationData":[OSD([subQ8,subQ7,subQ6,subQ5,subQ4,subQ1,sQuery(id+"F0.wireOp",EDGE,"E9"),sQuery(id+"F0.wireOp",EDGE,"E10.MirrorCS"),sQuery(id+"F0.wireOp",EDGE,"E11.1.0"),sQuery(id+"F0.wireOp",EDGE,"E11.1.1"),sQuery(id+"F0.wireOp",EDGE,"E11.2.0"),subQ0,subQ2,sQuery(id+"F0.wireOp",EDGE,"E11.3.1")])],"isStart":false});var subQ10=makeQuery(id+"F1.opExtrude","CAP_FACE",FACE,{"disambiguationData":[OSD([subQ8,subQ7,subQ6,subQ5,subQ4])],"isStart":false});var subQ11=makeQuery(id+"F9.opExtrude","SWEPT_FACE",FACE,{"disambiguationData":[OSD([sQuery(id+"F8.wireOp",EDGE,"E13.0")])]});var subQ12=sQuery(id+"F8.wireOp",EDGE,"E14");Q2=makeQuery(id+"F15.opChamfer","TWEAK_EDGE",EDGE,{"derivedFrom":[makeQuery(id+"F14.opFillet","BLEND_VERTEX",VERTEX,{"blendedFrom":[makeQuery(id+"F9.opExtrude","CAP_EDGE",EDGE,{"disambiguationData":[OSD([subQ12])],"isStart":false}),subQ3,makeQuery(id+"F2.boolean.opBoolean","MERGE",FACE,{"derivedFrom":[subQ10,subQ9]}),makeQuery(id+"F9.boolean.opBoolean","SPLIT",FACE,{"disambiguationData":[TD([subQ3])],"derivedFrom":subQ11})],"blendedInto":[subQ3,makeQuery(id+"F2.boolean.opBoolean","MERGE",FACE,{"derivedFrom":[subQ10,subQ9]}),makeQuery(id+"F9.boolean.opBoolean","SPLIT",FACE,{"disambiguationData":[TD([subQ3])],"derivedFrom":subQ11})]})]});}
            var Q3;
            {var subQ0=sQuery(id+"F0.wireOp",EDGE,"E11.3.0");var subQ1=makeQuery(id+"F2.opExtrude","SWEPT_FACE",FACE,{"disambiguationData":[OSD([subQ0])]});var subQ2=sQuery(id+"F0.wireOp",EDGE,"E7");var subQ3=sQuery(id+"F0.wireOp",EDGE,"E11.2.1");var subQ4=sQuery(id+"F0.wireOp",EDGE,"E6");var subQ5=sQuery(id+"F0.wireOp",EDGE,"E1.right");var subQ6=sQuery(id+"F0.wireOp",EDGE,"E1.left");var subQ7=sQuery(id+"F0.wireOp",EDGE,"E1.top");var subQ8=sQuery(id+"F0.wireOp",EDGE,"E1.bottom");var subQ9=makeQuery(id+"F2.opExtrude","CAP_FACE",FACE,{"disambiguationData":[OSD([subQ8,subQ7,subQ6,subQ5,subQ4,subQ2,sQuery(id+"F0.wireOp",EDGE,"E9"),sQuery(id+"F0.wireOp",EDGE,"E10.MirrorCS"),sQuery(id+"F0.wireOp",EDGE,"E11.1.0"),sQuery(id+"F0.wireOp",EDGE,"E11.1.1"),sQuery(id+"F0.wireOp",EDGE,"E11.2.0"),subQ3,subQ0,sQuery(id+"F0.wireOp",EDGE,"E11.3.1")])],"isStart":false});var subQ10=makeQuery(id+"F1.opExtrude","CAP_FACE",FACE,{"disambiguationData":[OSD([subQ8,subQ7,subQ6,subQ5,subQ4])],"isStart":false});var subQ11=makeQuery(id+"F9.opExtrude","SWEPT_FACE",FACE,{"disambiguationData":[OSD([sQuery(id+"F8.wireOp",EDGE,"E13.0")])]});var subQ12=sQuery(id+"F8.wireOp",EDGE,"E14");Q3=makeQuery(id+"F15.opChamfer","TWEAK_EDGE",EDGE,{"derivedFrom":[makeQuery(id+"F14.opFillet","BLEND_VERTEX",VERTEX,{"blendedFrom":[makeQuery(id+"F9.opExtrude","CAP_EDGE",EDGE,{"disambiguationData":[OSD([subQ12])],"isStart":true}),subQ1,makeQuery(id+"F2.boolean.opBoolean","MERGE",FACE,{"derivedFrom":[subQ10,subQ9]}),makeQuery(id+"F9.boolean.opBoolean","SPLIT",FACE,{"disambiguationData":[TD([subQ1])],"derivedFrom":subQ11})],"blendedInto":[subQ1,makeQuery(id+"F2.boolean.opBoolean","MERGE",FACE,{"derivedFrom":[subQ10,subQ9]}),makeQuery(id+"F9.boolean.opBoolean","SPLIT",FACE,{"disambiguationData":[TD([subQ1])],"derivedFrom":subQ11})]})]});}
            var Q4;
            {var subQ0=sQuery(id+"F0.wireOp",EDGE,"E11.3.1");var subQ1=makeQuery(id+"F2.opExtrude","SWEPT_FACE",FACE,{"disambiguationData":[OSD([subQ0])]});var subQ2=sQuery(id+"F0.wireOp",EDGE,"E6");var subQ3=sQuery(id+"F0.wireOp",EDGE,"E1.right");var subQ4=sQuery(id+"F0.wireOp",EDGE,"E1.left");var subQ5=sQuery(id+"F0.wireOp",EDGE,"E1.top");var subQ6=sQuery(id+"F0.wireOp",EDGE,"E1.bottom");var subQ7=makeQuery(id+"F1.opExtrude","CAP_FACE",FACE,{"disambiguationData":[OSD([subQ6,subQ5,subQ4,subQ3,subQ2])],"isStart":false});var subQ8=sQuery(id+"F0.wireOp",EDGE,"E7");var subQ9=sQuery(id+"F8.wireOp",EDGE,"E14");var subQ10=sQuery(id+"F8.wireOp",EDGE,"E13.0");var subQ11=sQuery(id+"F0.wireOp",EDGE,"E10.MirrorCS");var subQ12=makeQuery(id+"F2.opExtrude","CAP_FACE",FACE,{"disambiguationData":[OSD([subQ6,subQ5,subQ4,subQ3,subQ2,subQ8,sQuery(id+"F0.wireOp",EDGE,"E9"),subQ11,sQuery(id+"F0.wireOp",EDGE,"E11.1.0"),sQuery(id+"F0.wireOp",EDGE,"E11.1.1"),sQuery(id+"F0.wireOp",EDGE,"E11.2.0"),sQuery(id+"F0.wireOp",EDGE,"E11.2.1"),sQuery(id+"F0.wireOp",EDGE,"E11.3.0"),subQ0])],"isStart":false});var subQ13=makeQuery(id+"F9.opExtrude","SWEPT_FACE",FACE,{"disambiguationData":[OSD([subQ10])]});Q4=makeQuery(id+"F15.opChamfer","TWEAK_EDGE",EDGE,{"derivedFrom":[makeQuery(id+"F14.opFillet","BLEND_VERTEX",VERTEX,{"blendedFrom":[makeQuery(id+"F9.opExtrude","CAP_EDGE",EDGE,{"disambiguationData":[OSD([subQ9])],"isStart":true}),subQ1,makeQuery(id+"F2.boolean.opBoolean","MERGE",FACE,{"derivedFrom":[subQ7,subQ12]}),makeQuery(id+"F9.boolean.opBoolean","SPLIT",FACE,{"disambiguationData":[TD([subQ1])],"derivedFrom":subQ13})],"blendedInto":[subQ1,makeQuery(id+"F2.boolean.opBoolean","MERGE",FACE,{"derivedFrom":[subQ7,subQ12]}),makeQuery(id+"F9.boolean.opBoolean","SPLIT",FACE,{"disambiguationData":[TD([subQ1])],"derivedFrom":subQ13})]})]});}
            var Q5;
            {var subQ0=sQuery(id+"F0.wireOp",EDGE,"E10.MirrorCS");var subQ1=makeQuery(id+"F2.opExtrude","SWEPT_FACE",FACE,{"disambiguationData":[OSD([subQ0])]});var subQ2=sQuery(id+"F0.wireOp",EDGE,"E7");var subQ3=sQuery(id+"F0.wireOp",EDGE,"E11.3.1");var subQ4=sQuery(id+"F0.wireOp",EDGE,"E6");var subQ5=sQuery(id+"F0.wireOp",EDGE,"E1.right");var subQ6=sQuery(id+"F0.wireOp",EDGE,"E1.left");var subQ7=sQuery(id+"F0.wireOp",EDGE,"E1.top");var subQ8=sQuery(id+"F0.wireOp",EDGE,"E1.bottom");var subQ9=makeQuery(id+"F2.opExtrude","CAP_FACE",FACE,{"disambiguationData":[OSD([subQ8,subQ7,subQ6,subQ5,subQ4,subQ2,sQuery(id+"F0.wireOp",EDGE,"E9"),subQ0,sQuery(id+"F0.wireOp",EDGE,"E11.1.0"),sQuery(id+"F0.wireOp",EDGE,"E11.1.1"),sQuery(id+"F0.wireOp",EDGE,"E11.2.0"),sQuery(id+"F0.wireOp",EDGE,"E11.2.1"),sQuery(id+"F0.wireOp",EDGE,"E11.3.0"),subQ3])],"isStart":false});var subQ10=makeQuery(id+"F1.opExtrude","CAP_FACE",FACE,{"disambiguationData":[OSD([subQ8,subQ7,subQ6,subQ5,subQ4])],"isStart":false});var subQ11=sQuery(id+"F8.wireOp",EDGE,"E15");var subQ12=sQuery(id+"F8.wireOp",EDGE,"E13.0");var subQ13=makeQuery(id+"F9.opExtrude","SWEPT_FACE",FACE,{"disambiguationData":[OSD([subQ12])]});Q5=makeQuery(id+"F15.opChamfer","TWEAK_EDGE",EDGE,{"derivedFrom":[makeQuery(id+"F14.opFillet","BLEND_VERTEX",VERTEX,{"blendedFrom":[makeQuery(id+"F9.opExtrude","CAP_EDGE",EDGE,{"disambiguationData":[OSD([subQ11])],"isStart":true}),subQ1,makeQuery(id+"F2.boolean.opBoolean","MERGE",FACE,{"derivedFrom":[subQ10,subQ9]}),makeQuery(id+"F9.boolean.opBoolean","SPLIT",FACE,{"disambiguationData":[TD([subQ1])],"derivedFrom":subQ13})],"blendedInto":[subQ1,makeQuery(id+"F2.boolean.opBoolean","MERGE",FACE,{"derivedFrom":[subQ10,subQ9]}),makeQuery(id+"F9.boolean.opBoolean","SPLIT",FACE,{"disambiguationData":[TD([subQ1])],"derivedFrom":subQ13})]})]});}
            var Q6;
            {var subQ0=sQuery(id+"F0.wireOp",EDGE,"E9");var subQ1=makeQuery(id+"F2.opExtrude","SWEPT_FACE",FACE,{"disambiguationData":[OSD([subQ0])]});var subQ2=sQuery(id+"F0.wireOp",EDGE,"E7");var subQ3=sQuery(id+"F0.wireOp",EDGE,"E11.1.0");var subQ4=sQuery(id+"F0.wireOp",EDGE,"E6");var subQ5=sQuery(id+"F0.wireOp",EDGE,"E1.right");var subQ6=sQuery(id+"F0.wireOp",EDGE,"E1.left");var subQ7=sQuery(id+"F0.wireOp",EDGE,"E1.top");var subQ8=sQuery(id+"F0.wireOp",EDGE,"E1.bottom");var subQ9=makeQuery(id+"F2.opExtrude","CAP_FACE",FACE,{"disambiguationData":[OSD([subQ8,subQ7,subQ6,subQ5,subQ4,subQ2,subQ0,sQuery(id+"F0.wireOp",EDGE,"E10.MirrorCS"),subQ3,sQuery(id+"F0.wireOp",EDGE,"E11.1.1"),sQuery(id+"F0.wireOp",EDGE,"E11.2.0"),sQuery(id+"F0.wireOp",EDGE,"E11.2.1"),sQuery(id+"F0.wireOp",EDGE,"E11.3.0"),sQuery(id+"F0.wireOp",EDGE,"E11.3.1")])],"isStart":false});var subQ10=makeQuery(id+"F1.opExtrude","CAP_FACE",FACE,{"disambiguationData":[OSD([subQ8,subQ7,subQ6,subQ5,subQ4])],"isStart":false});var subQ11=sQuery(id+"F8.wireOp",EDGE,"E15");var subQ12=makeQuery(id+"F9.opExtrude","SWEPT_FACE",FACE,{"disambiguationData":[OSD([sQuery(id+"F8.wireOp",EDGE,"E13.0")])]});Q6=makeQuery(id+"F15.opChamfer","TWEAK_EDGE",EDGE,{"derivedFrom":[makeQuery(id+"F14.opFillet","BLEND_VERTEX",VERTEX,{"blendedFrom":[makeQuery(id+"F9.opExtrude","CAP_EDGE",EDGE,{"disambiguationData":[OSD([subQ11])],"isStart":true}),subQ1,makeQuery(id+"F2.boolean.opBoolean","MERGE",FACE,{"derivedFrom":[subQ10,subQ9]}),makeQuery(id+"F9.boolean.opBoolean","SPLIT",FACE,{"disambiguationData":[TD([subQ1])],"derivedFrom":subQ12})],"blendedInto":[subQ1,makeQuery(id+"F2.boolean.opBoolean","MERGE",FACE,{"derivedFrom":[subQ10,subQ9]}),makeQuery(id+"F9.boolean.opBoolean","SPLIT",FACE,{"disambiguationData":[TD([subQ1])],"derivedFrom":subQ12})]})]});}
            var Q7;
            {var subQ0=sQuery(id+"F0.wireOp",EDGE,"E11.1.0");var subQ1=makeQuery(id+"F2.opExtrude","SWEPT_FACE",FACE,{"disambiguationData":[OSD([subQ0])]});var subQ2=sQuery(id+"F0.wireOp",EDGE,"E9");var subQ3=sQuery(id+"F0.wireOp",EDGE,"E7");var subQ4=sQuery(id+"F0.wireOp",EDGE,"E6");var subQ5=sQuery(id+"F0.wireOp",EDGE,"E1.right");var subQ6=sQuery(id+"F0.wireOp",EDGE,"E1.left");var subQ7=sQuery(id+"F0.wireOp",EDGE,"E1.top");var subQ8=sQuery(id+"F0.wireOp",EDGE,"E1.bottom");var subQ9=makeQuery(id+"F2.opExtrude","CAP_FACE",FACE,{"disambiguationData":[OSD([subQ8,subQ7,subQ6,subQ5,subQ4,subQ3,subQ2,sQuery(id+"F0.wireOp",EDGE,"E10.MirrorCS"),subQ0,sQuery(id+"F0.wireOp",EDGE,"E11.1.1"),sQuery(id+"F0.wireOp",EDGE,"E11.2.0"),sQuery(id+"F0.wireOp",EDGE,"E11.2.1"),sQuery(id+"F0.wireOp",EDGE,"E11.3.0"),sQuery(id+"F0.wireOp",EDGE,"E11.3.1")])],"isStart":false});var subQ10=makeQuery(id+"F1.opExtrude","CAP_FACE",FACE,{"disambiguationData":[OSD([subQ8,subQ7,subQ6,subQ5,subQ4])],"isStart":false});var subQ11=makeQuery(id+"F9.opExtrude","SWEPT_FACE",FACE,{"disambiguationData":[OSD([sQuery(id+"F8.wireOp",EDGE,"E13.0")])]});var subQ12=sQuery(id+"F8.wireOp",EDGE,"E15");Q7=makeQuery(id+"F15.opChamfer","TWEAK_EDGE",EDGE,{"derivedFrom":[makeQuery(id+"F14.opFillet","BLEND_VERTEX",VERTEX,{"blendedFrom":[makeQuery(id+"F9.opExtrude","CAP_EDGE",EDGE,{"disambiguationData":[OSD([subQ12])],"isStart":false}),subQ1,makeQuery(id+"F2.boolean.opBoolean","MERGE",FACE,{"derivedFrom":[subQ10,subQ9]}),makeQuery(id+"F9.boolean.opBoolean","SPLIT",FACE,{"disambiguationData":[TD([subQ1])],"derivedFrom":subQ11})],"blendedInto":[subQ1,makeQuery(id+"F2.boolean.opBoolean","MERGE",FACE,{"derivedFrom":[subQ10,subQ9]}),makeQuery(id+"F9.boolean.opBoolean","SPLIT",FACE,{"disambiguationData":[TD([subQ1])],"derivedFrom":subQ11})]})]});}
            fillet(context, id + "F16", {"entities" : qUnion([Q0, Q1, Q2, Q3, Q4, Q5, Q6, Q7]), "radius" : 3.1 * mm, "allowEdgeOverflow" : false});
        }
        {
            var Q0;
            {var subQ0=sQuery(id+"F0.wireOp",EDGE,"E10.MirrorCS");var subQ8=sQuery(id+"F8.wireOp",EDGE,"E13.0");var subQ9=makeQuery(id+"F9.opExtrude","SWEPT_FACE",FACE,{"disambiguationData":[OSD([subQ8])]});Q0=makeQuery(id+"F9.boolean.opBoolean","SPLIT",FACE,{"disambiguationData":[TD([makeQuery(id+"F2.opExtrude","SWEPT_FACE",FACE,{"disambiguationData":[OSD([subQ0])]})])],"derivedFrom":subQ9});}
            var Q1;
            {var subQ0=sQuery(id+"F0.wireOp",EDGE,"E11.3.1");var subQ7=sQuery(id+"F8.wireOp",EDGE,"E13.0");var subQ9=makeQuery(id+"F9.opExtrude","SWEPT_FACE",FACE,{"disambiguationData":[OSD([subQ7])]});Q1=makeQuery(id+"F9.boolean.opBoolean","SPLIT",FACE,{"disambiguationData":[TD([makeQuery(id+"F2.opExtrude","SWEPT_FACE",FACE,{"disambiguationData":[OSD([subQ0])]})])],"derivedFrom":subQ9});}
            var Q2;
            {var subQ0=sQuery(id+"F0.wireOp",EDGE,"E9");var subQ8=makeQuery(id+"F9.opExtrude","SWEPT_FACE",FACE,{"disambiguationData":[OSD([sQuery(id+"F8.wireOp",EDGE,"E13.0")])]});Q2=makeQuery(id+"F9.boolean.opBoolean","SPLIT",FACE,{"disambiguationData":[TD([makeQuery(id+"F2.opExtrude","SWEPT_FACE",FACE,{"disambiguationData":[OSD([subQ0])]})])],"derivedFrom":subQ8});}
            var Q3;
            {var subQ0=sQuery(id+"F0.wireOp",EDGE,"E11.1.0");var subQ8=makeQuery(id+"F9.opExtrude","SWEPT_FACE",FACE,{"disambiguationData":[OSD([sQuery(id+"F8.wireOp",EDGE,"E13.0")])]});Q3=makeQuery(id+"F9.boolean.opBoolean","SPLIT",FACE,{"disambiguationData":[TD([makeQuery(id+"F2.opExtrude","SWEPT_FACE",FACE,{"disambiguationData":[OSD([subQ0])]})])],"derivedFrom":subQ8});}
            var Q4;
            {var subQ0=sQuery(id+"F0.wireOp",EDGE,"E11.1.1");var subQ8=sQuery(id+"F8.wireOp",EDGE,"E13.0");var subQ9=makeQuery(id+"F9.opExtrude","SWEPT_FACE",FACE,{"disambiguationData":[OSD([subQ8])]});Q4=makeQuery(id+"F9.boolean.opBoolean","SPLIT",FACE,{"disambiguationData":[TD([makeQuery(id+"F2.opExtrude","SWEPT_FACE",FACE,{"disambiguationData":[OSD([subQ0])]})])],"derivedFrom":subQ9});}
            var Q5;
            {var subQ0=sQuery(id+"F0.wireOp",EDGE,"E11.2.0");var subQ1=sQuery(id+"F8.wireOp",EDGE,"E13.0");var subQ2=makeQuery(id+"F9.opExtrude","SWEPT_FACE",FACE,{"disambiguationData":[OSD([subQ1])]});Q5=makeQuery(id+"F9.boolean.opBoolean","SPLIT",FACE,{"disambiguationData":[TD([makeQuery(id+"F2.opExtrude","SWEPT_FACE",FACE,{"disambiguationData":[OSD([subQ0])]})])],"derivedFrom":subQ2});}
            var Q6;
            {var subQ0=sQuery(id+"F0.wireOp",EDGE,"E11.2.1");var subQ8=makeQuery(id+"F9.opExtrude","SWEPT_FACE",FACE,{"disambiguationData":[OSD([sQuery(id+"F8.wireOp",EDGE,"E13.0")])]});Q6=makeQuery(id+"F9.boolean.opBoolean","SPLIT",FACE,{"disambiguationData":[TD([makeQuery(id+"F2.opExtrude","SWEPT_FACE",FACE,{"disambiguationData":[OSD([subQ0])]})])],"derivedFrom":subQ8});}
            var Q7;
            {var subQ0=sQuery(id+"F0.wireOp",EDGE,"E11.3.0");var subQ8=makeQuery(id+"F9.opExtrude","SWEPT_FACE",FACE,{"disambiguationData":[OSD([sQuery(id+"F8.wireOp",EDGE,"E13.0")])]});Q7=makeQuery(id+"F9.boolean.opBoolean","SPLIT",FACE,{"disambiguationData":[TD([makeQuery(id+"F2.opExtrude","SWEPT_FACE",FACE,{"disambiguationData":[OSD([subQ0])]})])],"derivedFrom":subQ8});}
            var Q8;
            {var subQ0=sQuery(id+"F0.wireOp",EDGE,"E6");var subQ1=sQuery(id+"F0.wireOp",EDGE,"E1.right");var subQ2=sQuery(id+"F0.wireOp",EDGE,"E1.left");var subQ3=sQuery(id+"F0.wireOp",EDGE,"E1.top");var subQ4=sQuery(id+"F0.wireOp",EDGE,"E1.bottom");Q8=makeQuery(id+"F2.boolean.opBoolean","MERGE",FACE,{"derivedFrom":[makeQuery(id+"F1.opExtrude","CAP_FACE",FACE,{"disambiguationData":[OSD([subQ4,subQ3,subQ2,subQ1,subQ0])],"isStart":true}),makeQuery(id+"F2.opExtrude","CAP_FACE",FACE,{"disambiguationData":[OSD([subQ4,subQ3,subQ2,subQ1,subQ0,sQuery(id+"F0.wireOp",EDGE,"E7"),sQuery(id+"F0.wireOp",EDGE,"E9"),sQuery(id+"F0.wireOp",EDGE,"E10.MirrorCS"),sQuery(id+"F0.wireOp",EDGE,"E11.1.0"),sQuery(id+"F0.wireOp",EDGE,"E11.1.1"),sQuery(id+"F0.wireOp",EDGE,"E11.2.0"),sQuery(id+"F0.wireOp",EDGE,"E11.2.1"),sQuery(id+"F0.wireOp",EDGE,"E11.3.0"),sQuery(id+"F0.wireOp",EDGE,"E11.3.1")])],"isStart":true})]});}
            extrude(context, id + "F17", {"entities" : qUnion([Q0, Q1, Q2, Q3, Q4, Q5, Q6, Q7]), "operationType" : NewBodyOperationType.ADD, "endBound" : BoundingType.UP_TO_SURFACE, "endBoundEntityFace" : qUnion([Q8]), "depth" : 25 * mm});
        }
    });
